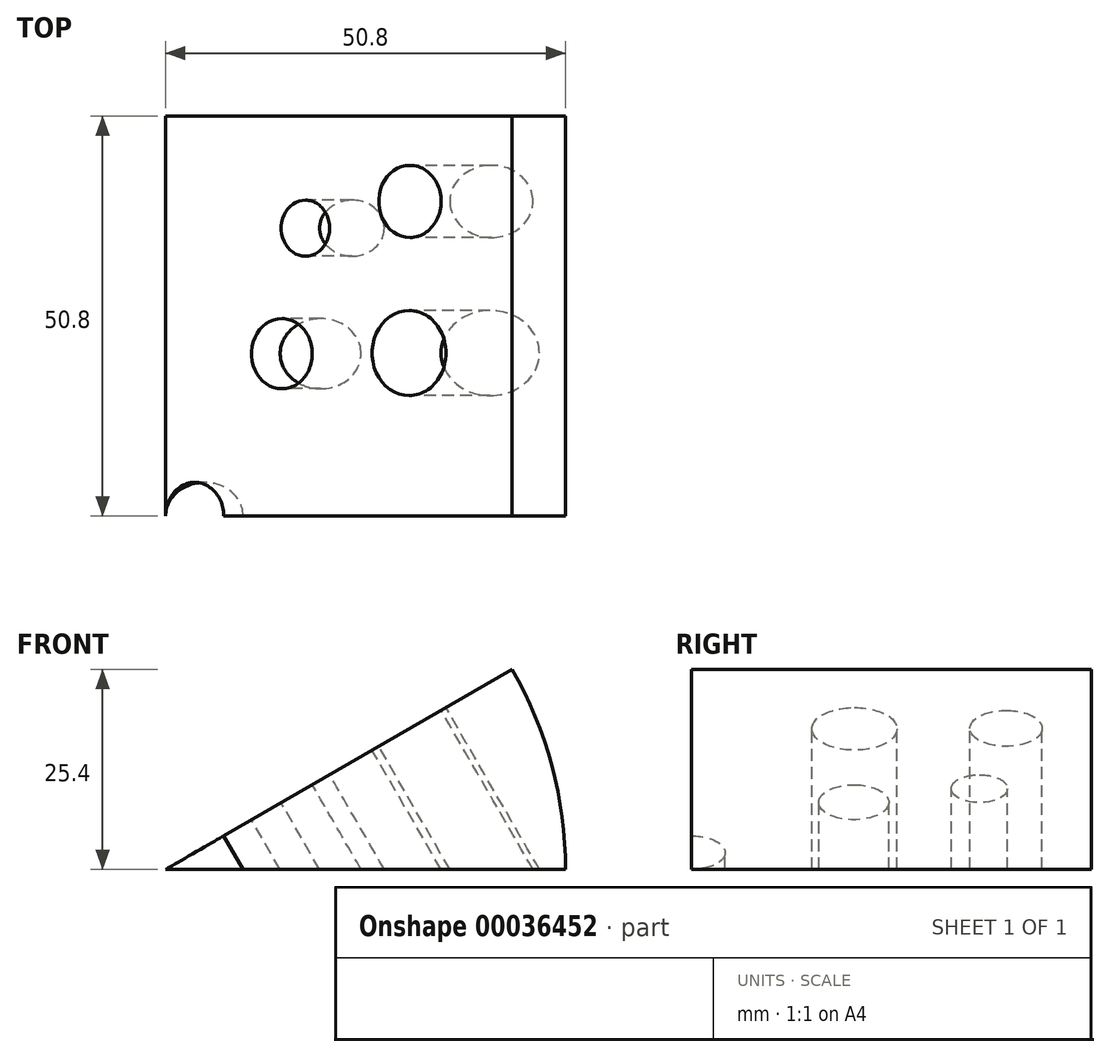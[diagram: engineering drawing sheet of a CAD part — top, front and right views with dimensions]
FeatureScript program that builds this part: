
annotation { "Feature Type Name" : "Feature", "Feature Type Description" : "" }
export const myFeature = defineFeature(function(context is Context, id is Id, definition is map)
    precondition{}
    {
        {
            var Q0;
            Q0=qCreatedBy(makeId("Top.planeOp"),FACE);
            var sketch = newSketch(context, id + "F0", { "sketchPlane" : qUnion([Q0])});
            skLineSegment(sketch, "E0.bottom", {"start": v(0, 50.8) * mm, "end": v(50.8, 50.8) * mm});
            skLineSegment(sketch, "E0.top", {"start": v(0, 0) * mm, "end": v(50.8, 0) * mm});
            skLineSegment(sketch, "E0.left", {"start": v(0, 50.8) * mm, "end": v(0, 0) * mm});
            skLineSegment(sketch, "E0.right", {"start": v(50.8, 50.8) * mm, "end": v(50.8, 0) * mm});
            skSolve(sketch);
        }
        {
            var Q0;
            Q0=qCreatedBy(makeId("Top.planeOp"),FACE);
            var sketch = newSketch(context, id + "F1", { "sketchPlane" : qUnion([Q0])});
            skLineSegment(sketch, "E1", {"start": v(0, 0) * mm, "end": v(0, 66.36) * mm});
            skSolve(sketch);
        }
        {
            var Q0;
            Q0 = qSketchRegion(id + "F0", true);
            var Q1;
            Q1=sQuery(id+"F1.wireOp",EDGE,"E1");
            revolve(context, id + "F2", {"entities" : qUnion([Q0]), "axis" : qUnion([Q1]), "revolveType" : RevolveType.ONE_DIRECTION, "oppositeDirection" : true, "angle" : 30 * degree});
        }
        {
            var Q0;
            Q0=makeQuery(id+"F2.opRevolve","CAP_FACE",FACE,{"disambiguationData":[OSD([sQuery(id+"F0.wireOp",EDGE,"E0.bottom"),sQuery(id+"F0.wireOp",EDGE,"E0.top"),sQuery(id+"F0.wireOp",EDGE,"E0.left"),sQuery(id+"F0.wireOp",EDGE,"E0.right")])],"isStart":false});
            var sketch = newSketch(context, id + "F3", { "sketchPlane" : qUnion([Q0])});
            skCircle(sketch, "E2", {"center": v(17.06, 20.62) * mm, "radius": 4.45 * mm});
            skCircle(sketch, "E3", {"center": v(35.7, 20.7) * mm, "radius": 5.41 * mm});
            skCircle(sketch, "E4", {"center": v(20.5, 36.56) * mm, "radius": 3.56 * mm});
            skCircle(sketch, "E5", {"center": v(4.26, 0) * mm, "radius": 4.26 * mm});
            skCircle(sketch, "E6", {"center": v(35.84, 39.97) * mm, "radius": 4.58 * mm});
            skSolve(sketch);
        }
        {
            var Q0;
            Q0 = qSketchRegion(id + "F3", true);
            extrude(context, id + "F4", {"entities" : qUnion([Q0]), "operationType" : NewBodyOperationType.REMOVE, "oppositeDirection" : true, "depth" : 25.4 * mm});
        }
    });
